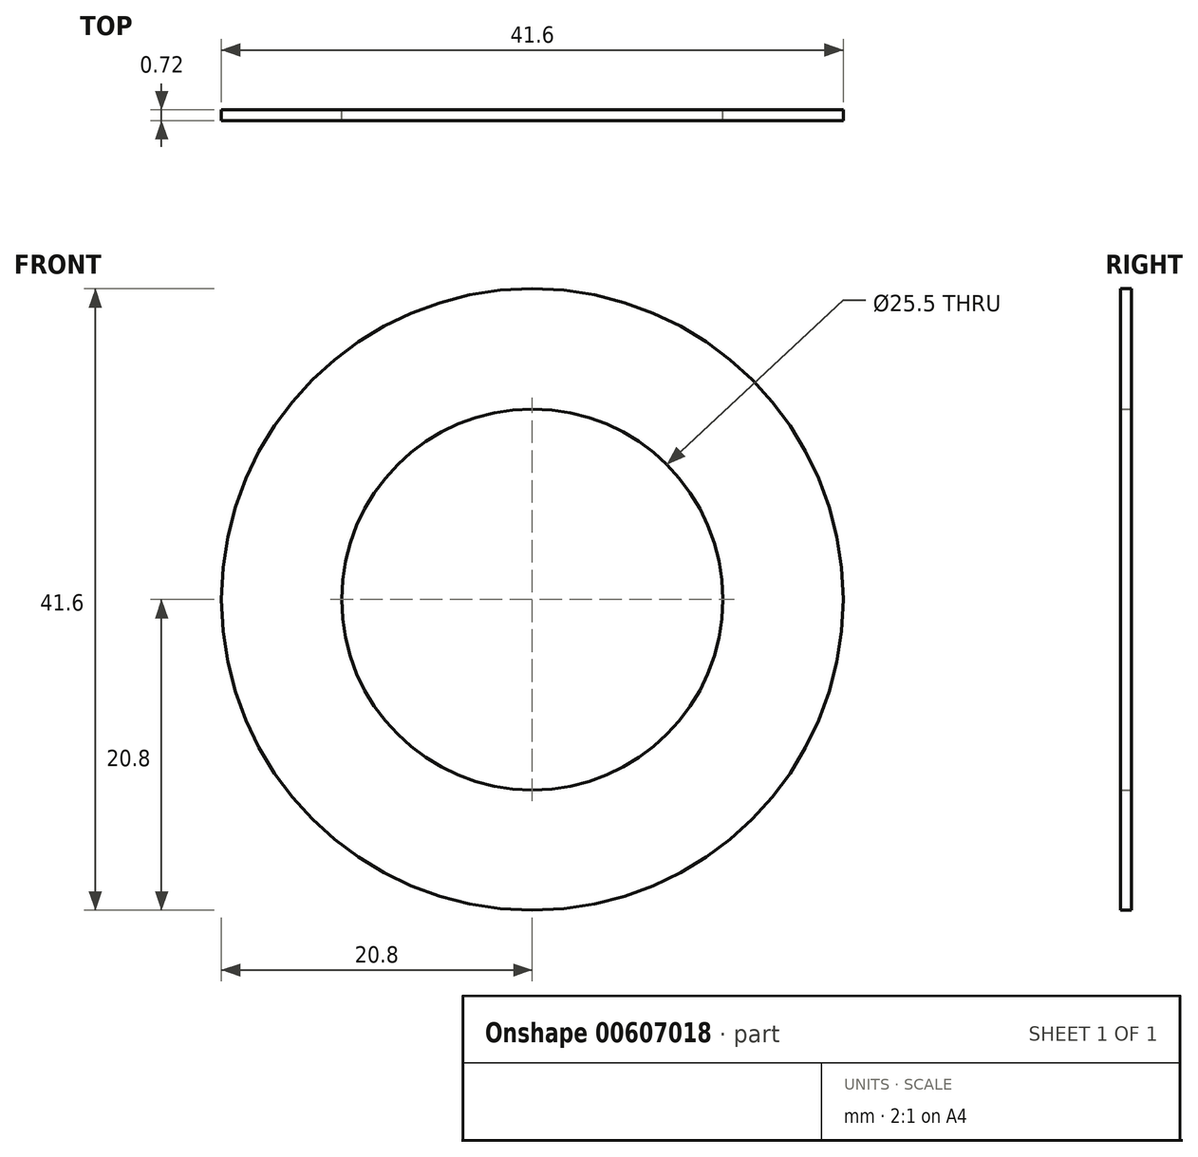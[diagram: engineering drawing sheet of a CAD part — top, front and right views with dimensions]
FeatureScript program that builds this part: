
annotation { "Feature Type Name" : "Feature", "Feature Type Description" : "" }
export const myFeature = defineFeature(function(context is Context, id is Id, definition is map)
    precondition{}
    {
        {
            var Q0;
            Q0=qCreatedBy(makeId("Front.planeOp"),FACE);
            var sketch = newSketch(context, id + "F0", { "sketchPlane" : qUnion([Q0]) });
            skCircle(sketch, "E0", {"center": v(0, 0) * mm, "radius": 20.8 * mm});
            skCircle(sketch, "E1", {"center": v(0, 0) * mm, "radius": 12.75 * mm});
            skSolve(sketch);
        }
        {
            var Q0;
            Q0=makeQuery(id+"F0.imprint","IMPRINT",FACE,{"disambiguationData":[TD([[makeQuery(id+"F0.imprint","IMPRINT",EDGE,{"derivedFrom":sQuery(id+"F0.wireOp",EDGE,"E0")}),1.0]])]});
            extrude(context, id + "F1", {"entities" : qUnion([Q0]), "depth" : 0.72 * mm, "offsetDistance" : 25 * mm});
        }
    });
